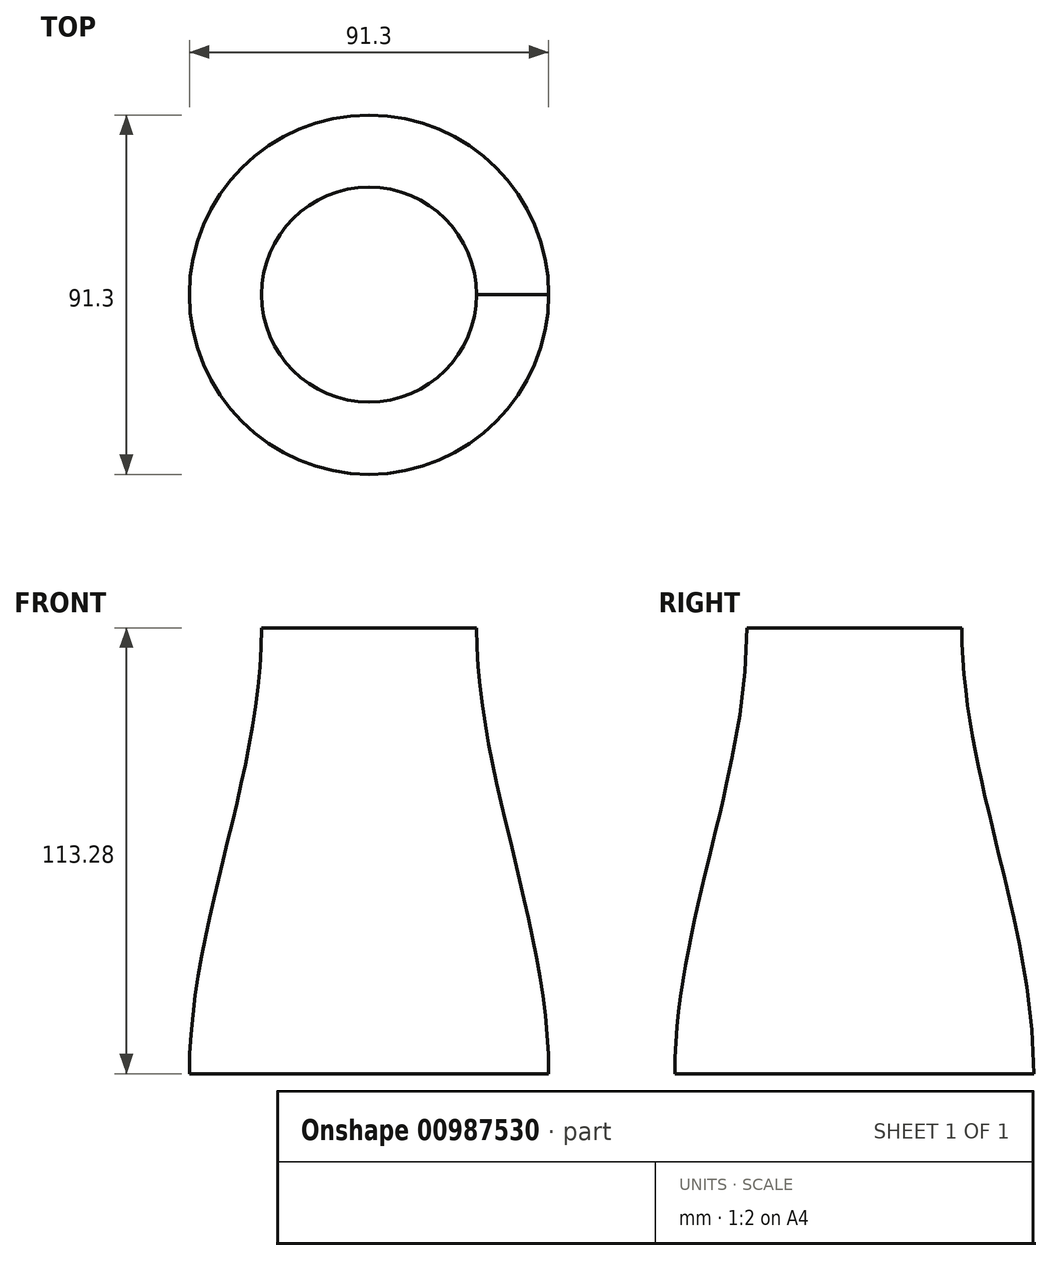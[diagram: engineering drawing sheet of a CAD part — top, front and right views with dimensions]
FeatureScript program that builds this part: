
annotation { "Feature Type Name" : "Feature", "Feature Type Description" : "" }
export const myFeature = defineFeature(function(context is Context, id is Id, definition is map)
    precondition{}
    {
        {
            var Q0;
            Q0=qCreatedBy(makeId("Top.planeOp"),FACE);
            var sketch = newSketch(context, id + "F0", { "sketchPlane" : qUnion([Q0])});
            skCircle(sketch, "E0", {"center": v(0, 0) * mm, "radius": 45.65 * mm});
            skSolve(sketch);
        }
        {
            var Q0;
            Q0=qCreatedBy(makeId("Top.planeOp"),FACE);
            cPlane(context, id + "F1", {"entities" : qUnion([Q0]), "cplaneType" : CPlaneType.OFFSET, "offset" : 113.28 * mm, "width" : 152.4 * mm, "height" : 152.4 * mm});
        }
        {
            var Q0;
            Q0=qCreatedBy(id+"F1.planeOp",FACE);
            var sketch = newSketch(context, id + "F2", { "sketchPlane" : qUnion([Q0])});
            skCircle(sketch, "E1", {"center": v(0, 0) * mm, "radius": 27.3 * mm});
            skSolve(sketch);
        }
        {
            var Q0;
            Q0=makeQuery(id+"F2.imprint","IMPRINT",FACE,{"disambiguationData":[TD([[makeQuery(id+"F2.imprint","IMPRINT",EDGE,{"derivedFrom":sQuery(id+"F2.wireOp",EDGE,"E1")}),1.0]])]});
            var Q1;
            Q1=makeQuery(id+"F0.imprint","IMPRINT",FACE,{"disambiguationData":[TD([[makeQuery(id+"F0.imprint","IMPRINT",EDGE,{"derivedFrom":sQuery(id+"F0.wireOp",EDGE,"E0")}),1.0]])]});
            loft(context, id + "F3", {"startCondition" : LoftEndDerivativeType.NORMAL_TO_PROFILE, "startMagnitude" : 1, "endCondition" : LoftEndDerivativeType.NORMAL_TO_PROFILE, "endMagnitude" : 1, "sheetProfilesArray" : [{ "sheetProfileEntities" : qUnion([Q0]) }, { "sheetProfileEntities" : qUnion([Q1]) }]});
        }
    });
